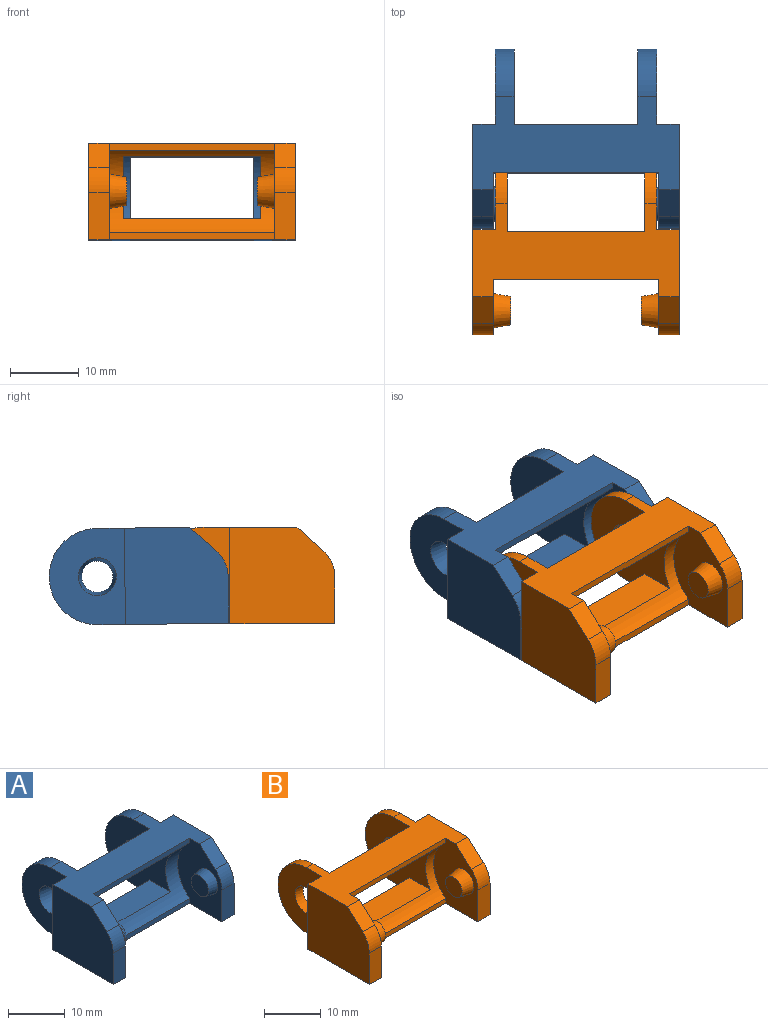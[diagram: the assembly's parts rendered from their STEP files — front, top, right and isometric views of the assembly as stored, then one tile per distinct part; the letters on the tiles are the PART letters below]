
ASSEMBLY  parts=2 mates=1
PART A: 34 faces, bbox 30x26x14 mm
  f0: plane 16.91x14mm, normal (-1,0,0), area 157.2mm2, adj f2,f4,f8,f11,f14,f17,f18,f19
  f1: plane 6.79x3mm, normal (0,-1,0), area 20.4mm2, adj f2,f6,f7,f13
  f2: plane 30x19mm, normal (0,0,-1), area 279.6mm2, adj f0,f1,f3,f7,f8,f9,f10,f13
  f3: plane 14x3.3mm, normal (0,1,0), area 46.2mm2, adj f2,f4,f7,f9
  f4: plane 30x13.5mm, normal (0,0,1), area 246.6mm2, adj f0,f3,f5,f7,f8,f9,f12,f13
  f5: plane 3.86x3.51mm, normal (0,-0.67,0.74), area 15.7mm2, adj f4,f6,f7,f13
  f6: cylinder r=5mm len=3.7mm, axis (-1,0,0), area 12.5mm2, adj f1,f5,f7,f13
  f7: plane 15x14mm, normal (1,0,0), area 195.6mm2, adj f1,f2,f3,f4,f5,f6
  f8: cylinder r=7mm len=14mm, axis (-1,0,0), area 59.4mm2, adj f0,f2,f4,f9
  f9: plane 14x11mm, normal (1,0,0), area 109.2mm2, adj f2,f3,f4,f8,f14
  f10: plane 24x1mm, normal (0,-1,0), area 24mm2, adj f2,f11,f13,f29
  f11: cylinder r=7.5mm len=24mm, axis (-1,0,0), area 159.4mm2, adj f0,f10,f12,f13,f17,f20,f21,f29
  f12: plane 24x1mm, normal (0,-1,0), area 24mm2, adj f4,f11,f13,f29
  f13: plane 14x11mm, normal (-1,0,0), area 103.1mm2, adj f1,f2,f4,f5,f6,f10,f11,f12
  f14: cone r=2.75mm half-angle=10deg, axis (1,0,0), area 43.3mm2, adj f0,f9
  f15: cone r=2.5mm half-angle=10deg, axis (1,0,0), area 29.7mm2, adj f13,f16
  f16: plane 4.29x4.29mm, normal (-1,0,0), area 14.5mm2, adj f15
  f17: plane 18x5.16mm, normal (0,0,1), area 92.8mm2, adj f0,f11,f18,f21
  f18: plane 18x3mm, normal (0,1,0), area 54mm2, adj f0,f2,f17,f21
  f19: plane 18x2mm, normal (0,1,0), area 36mm2, adj f0,f4,f20,f21
  f20: plane 18x5.91mm, normal (0,0,-1), area 106.4mm2, adj f0,f11,f19,f21
  f21: plane 16.91x14mm, normal (1,0,0), area 157.2mm2, adj f2,f4,f11,f17,f18,f19,f20,f27
  f22: plane 6.79x3mm, normal (0,-1,0), area 20.4mm2, adj f2,f25,f26,f29
  f23: plane 14x3.3mm, normal (0,1,0), area 46.2mm2, adj f2,f4,f26,f28
  f24: plane 3.86x3.51mm, normal (0,-0.67,0.74), area 15.7mm2, adj f4,f25,f26,f29
  f25: cylinder r=5mm len=3.7mm, axis (1,0,0), area 12.5mm2, adj f22,f24,f26,f29
  f26: plane 15x14mm, normal (-1,0,0), area 195.6mm2, adj f2,f4,f22,f23,f24,f25
  f27: cylinder r=7mm len=14mm, axis (1,0,0), area 59.4mm2, adj f2,f4,f21,f28
  f28: plane 14x11mm, normal (-1,0,0), area 109.2mm2, adj f2,f4,f23,f27,f30
  f29: plane 14x11mm, normal (1,0,0), area 103.1mm2, adj f2,f4,f10,f11,f12,f22,f24,f25
  f30: cone r=2.75mm half-angle=10deg, axis (-1,0,0), area 43.3mm2, adj f21,f28
  f31: cone r=2.5mm half-angle=10deg, axis (-1,0,0), area 17.9mm2, adj f29,f33
  f32: plane 2.62x2.62mm, normal (1,0,0), area 5.4mm2, adj f33
  f33: torus R=1.31mm, axis (1,0,0), area 16.7mm2, adj f31,f32
PART B: 33 faces, bbox 30x26x14 mm
  f0: plane 16.91x14mm, normal (-1,0,0), area 154.6mm2, adj f2,f4,f8,f11,f14,f17,f18,f19
  f1: plane 6.79x3mm, normal (0,-1,0), area 20.4mm2, adj f2,f6,f7,f13
  f2: plane 30x19mm, normal (0,0,-1), area 273.2mm2, adj f0,f1,f3,f7,f8,f9,f10,f13
  f3: plane 14x3.3mm, normal (0,1,0), area 46.2mm2, adj f2,f4,f7,f9
  f4: plane 30x13.5mm, normal (0,0,1), area 240.3mm2, adj f0,f3,f5,f7,f8,f9,f12,f13
  f5: plane 3.86x3.51mm, normal (0,-0.67,0.74), area 15.7mm2, adj f4,f6,f7,f13
  f6: cylinder r=5mm len=3.7mm, axis (-1,0,0), area 12.5mm2, adj f1,f5,f7,f13
  f7: plane 15.25x14mm, normal (1,0,0), area 199.1mm2, adj f1,f2,f3,f4,f5,f6
  f8: cylinder r=7mm len=14mm, axis (-1,0,0), area 37.4mm2, adj f0,f2,f4,f9
  f9: plane 14x10.75mm, normal (1,0,0), area 105.7mm2, adj f2,f3,f4,f8,f14
  f10: plane 24x1mm, normal (0,-1,0), area 24mm2, adj f2,f11,f13,f29
  f11: cylinder r=7.5mm len=24mm, axis (-1,0,0), area 140mm2, adj f0,f10,f12,f13,f17,f20,f21,f29
  f12: plane 24x1mm, normal (0,-1,0), area 24mm2, adj f4,f11,f13,f29
  f13: plane 14x11mm, normal (-1,0,0), area 103.1mm2, adj f1,f2,f4,f5,f6,f10,f11,f12
  f14: cone r=2.75mm half-angle=10deg, axis (1,0,0), area 28.2mm2, adj f0,f9
  f15: cone r=2.5mm half-angle=10deg, axis (1,0,0), area 36.4mm2, adj f13,f16
  f16: plane 4.12x4.12mm, normal (-1,0,0), area 13.3mm2, adj f15
  f17: plane 20x5.16mm, normal (0,0,1), area 103.1mm2, adj f0,f11,f18,f21
  f18: plane 20x3mm, normal (0,1,0), area 60mm2, adj f0,f2,f17,f21
  f19: plane 20x2mm, normal (0,1,0), area 40mm2, adj f0,f4,f20,f21
  f20: plane 20x5.91mm, normal (0,0,-1), area 118.2mm2, adj f0,f11,f19,f21
  f21: plane 16.91x14mm, normal (1,0,0), area 154.6mm2, adj f2,f4,f11,f17,f18,f19,f20,f27
  f22: plane 6.79x3mm, normal (0,-1,0), area 20.4mm2, adj f2,f25,f26,f29
  f23: plane 14x3.3mm, normal (0,1,0), area 46.2mm2, adj f2,f4,f26,f28
  f24: plane 3.86x3.51mm, normal (0,-0.67,0.74), area 15.7mm2, adj f4,f25,f26,f29
  f25: cylinder r=5mm len=3.7mm, axis (1,0,0), area 12.5mm2, adj f22,f24,f26,f29
  f26: plane 15.25x14mm, normal (-1,0,0), area 199.1mm2, adj f2,f4,f22,f23,f24,f25
  f27: cylinder r=7mm len=14mm, axis (1,0,0), area 37.4mm2, adj f2,f4,f21,f28
  f28: plane 14x10.75mm, normal (-1,0,0), area 105.7mm2, adj f2,f4,f23,f27,f30
  f29: plane 14x11mm, normal (1,0,0), area 103.1mm2, adj f2,f4,f10,f11,f12,f22,f24,f25
  f30: cone r=2.75mm half-angle=10deg, axis (-1,0,0), area 28.2mm2, adj f21,f28
  f31: cone r=2.5mm half-angle=10deg, axis (-1,0,0), area 36.4mm2, adj f29,f32
  f32: plane 4.12x4.12mm, normal (1,0,0), area 13.3mm2, adj f31
PLACE A rot(axis=(-1,0,0),0.7deg) t=(-0.39,12.96,-0.01)mm
PLACE B t=(-0.39,-2.54,0.11)mm fixed
MATE revolute A.f15 <-> B.f14  axis (1,0,0) through (-10.39,3.46,0.11)mm
